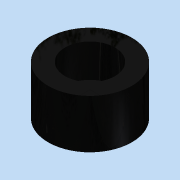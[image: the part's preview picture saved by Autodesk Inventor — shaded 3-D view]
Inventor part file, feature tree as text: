
AUTODESK INVENTOR PART (.ipt)
format: ipt  version: 2015 (Build 190159000, 159)  size: 91,648 bytes
history: native  units: in
note: dims shown in document units (in); Inventor stores cm internally (conversion verified against a paired STEP export)
features: extrude x2, sketch x2
ambient origin geometry x8: Origin, YZ Plane, XZ Plane, XY Plane, X Axis, Y Axis, Z Axis, Center Point
bodies: Solid1 (feature_tree)
feature tree (4):
  extrude  "Extrusion1"  Depth=0.1875in
  extrude  "Extrusion2"  Depth=0.0591in TaperAngle=0.0deg
  sketch  "Sketch1"  dims[d0=0.315in d1=0.1875in]
  sketch  "Sketch2"  dims[d2=0.125in d3=0.0in d4=0.0591in d5=0.0in]
